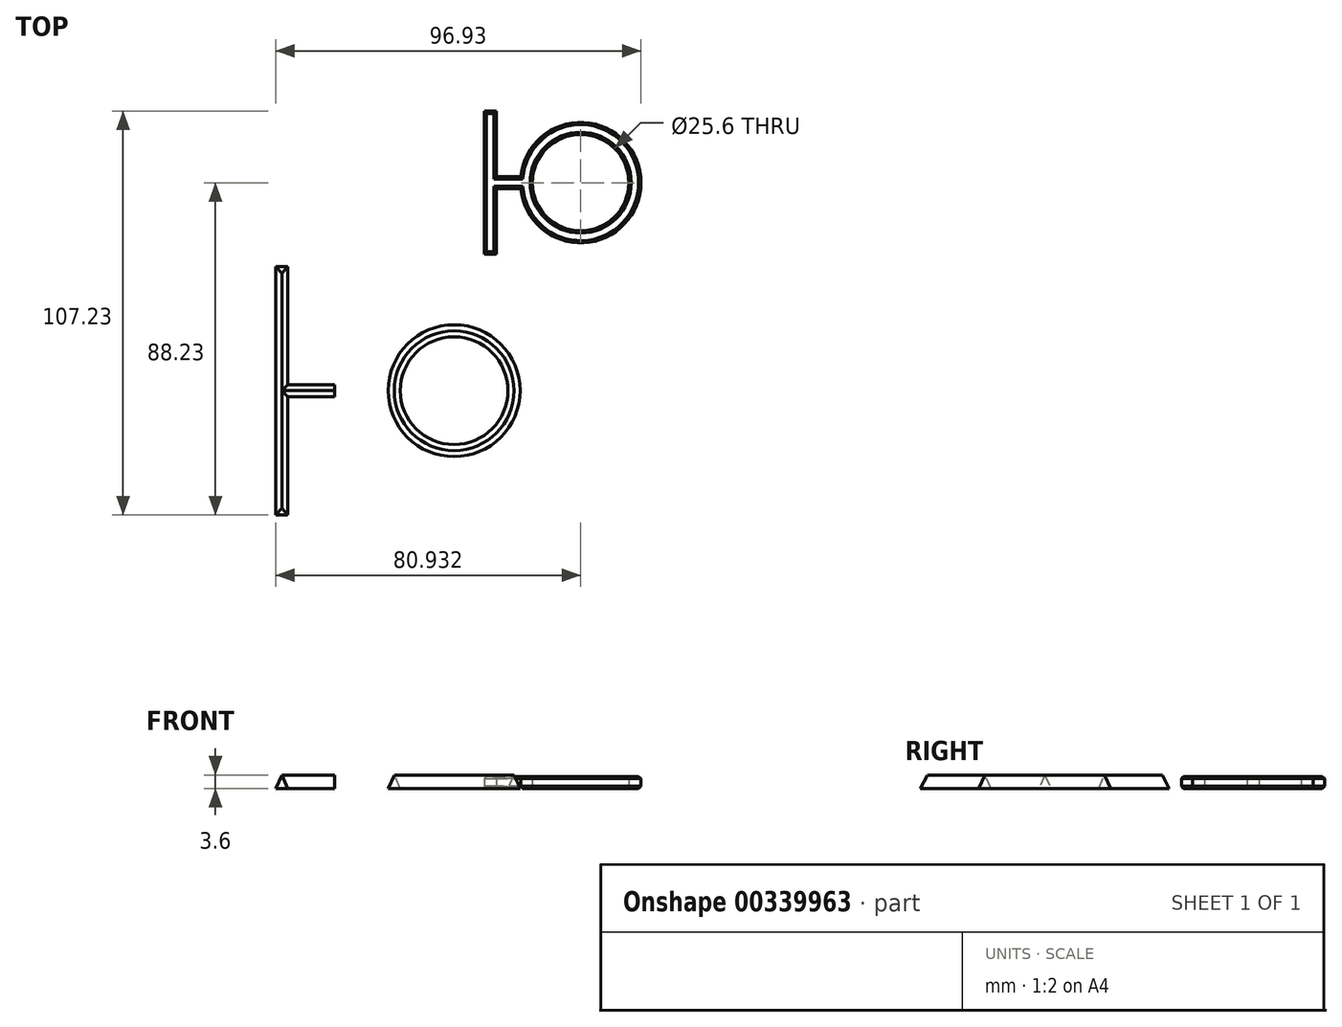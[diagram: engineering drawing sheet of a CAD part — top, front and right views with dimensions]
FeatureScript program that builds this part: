
annotation { "Feature Type Name" : "Feature", "Feature Type Description" : "" }
export const myFeature = defineFeature(function(context is Context, id is Id, definition is map)
    precondition{}
    {
        {
            var Q0;
            Q0=qCreatedBy(makeId("Top.planeOp"),FACE);
            var sketch = newSketch(context, id + "F0", { "sketchPlane" : qUnion([Q0])});
            skCircle(sketch, "E0", {"center": v(0, 0) * mm, "radius": 17.5 * mm});
            skCircle(sketch, "E1", {"center": v(0, 0) * mm, "radius": 14.3 * mm});
            skLineSegment(sketch, "E2.bottom", {"start": v(-45.75, 1.6) * mm, "end": v(-31.75, 1.6) * mm});
            skLineSegment(sketch, "E2.top", {"start": v(-45.75, -1.6) * mm, "end": v(-31.75, -1.6) * mm});
            skLineSegment(sketch, "E2.left", {"start": v(-45.75, 1.6) * mm, "end": v(-45.75, -1.6) * mm});
            skLineSegment(sketch, "E2.right", {"start": v(-31.75, 1.6) * mm, "end": v(-31.75, -1.6) * mm});
            skPoint(sketch, "E2.middle", {"position": v(-38.75, 0) * mm});
            skLineSegment(sketch, "E3.bottom", {"start": v(-47.35, 33) * mm, "end": v(-44.15, 33) * mm});
            skLineSegment(sketch, "E3.top", {"start": v(-47.35, -33) * mm, "end": v(-44.15, -33) * mm});
            skLineSegment(sketch, "E3.left", {"start": v(-47.35, 33) * mm, "end": v(-47.35, -33) * mm});
            skLineSegment(sketch, "E3.right", {"start": v(-44.15, 33) * mm, "end": v(-44.15, -33) * mm});
            skPoint(sketch, "E3.middle", {"position": v(-45.75, 0) * mm});
            skSolve(sketch);
        }
        {
            var Q0;
            Q0 = qSketchRegion(id + "F0", true);
            extrude(context, id + "F1", {"entities" : qUnion([Q0]), "depth" : 3.6 * mm, "offsetDistance" : 25 * mm});
        }
        {
            var Q0;
            Q0=makeQuery(id+"F1.opExtrude","CAP_EDGE",EDGE,{"disambiguationData":[OSD([sQuery(id+"F0.wireOp",EDGE,"E1")])],"isStart":false});
            var Q1;
            Q1=makeQuery(id+"F1.opExtrude","CAP_EDGE",EDGE,{"disambiguationData":[OSD([sQuery(id+"F0.wireOp",EDGE,"E0")])],"isStart":false});
            chamfer(context, id + "F2", {"entities" : qUnion([Q0, Q1]), "chamferType" : ChamferType.TWO_OFFSETS, "width1" : 3.6 * mm, "oppositeDirection" : false, "width2" : 1.6 * mm, "tangentPropagation" : true});
        }
        {
            var Q0;
            Q0=makeQuery(id+"F1.opExtrude","CAP_EDGE",EDGE,{"disambiguationData":[OSD([sQuery(id+"F0.wireOp",EDGE,"E3.top")])],"isStart":false});
            var Q1;
            Q1=makeQuery(id+"F1.opExtrude","CAP_EDGE",EDGE,{"disambiguationData":[OSD([sQuery(id+"F0.wireOp",EDGE,"E3.bottom")])],"isStart":false});
            chamfer(context, id + "F3", {"entities" : qUnion([Q0, Q1]), "chamferType" : ChamferType.TWO_OFFSETS, "width1" : 1.8 * mm, "oppositeDirection" : false, "width2" : 3.6 * mm, "tangentPropagation" : true});
        }
        {
            var Q0;
            Q0=makeQuery(id+"F1.opExtrude","CAP_EDGE",EDGE,{"disambiguationData":[OSD([sQuery(id+"F0.wireOp",EDGE,"E3.left")])],"isStart":false});
            var Q1;
            {var subQ0=sQuery(id+"F0.wireOp",EDGE,"E3.right");Q1=makeQuery(id+"F1.opExtrude","CAP_EDGE",EDGE,{"disambiguationData":[OSD([subQ0]),TDD([makeQuery(id+"F0.imprint","IMPRINT",EDGE,{"disambiguationData":[TD([[makeQuery(id+"F0.imprint","INTERSECT",VERTEX,{"derivedFrom":[sQuery(id+"F0.wireOp",EDGE,"E3.bottom"),subQ0]}),-1.0]])],"derivedFrom":subQ0})])],"isStart":false});}
            var Q2;
            {var subQ0=sQuery(id+"F0.wireOp",EDGE,"E3.right");Q2=makeQuery(id+"F1.opExtrude","CAP_EDGE",EDGE,{"disambiguationData":[OSD([subQ0]),TDD([makeQuery(id+"F0.imprint","IMPRINT",EDGE,{"disambiguationData":[TD([[makeQuery(id+"F0.imprint","INTERSECT",VERTEX,{"derivedFrom":[sQuery(id+"F0.wireOp",EDGE,"E3.top"),subQ0]}),1.0]])],"derivedFrom":subQ0})])],"isStart":false});}
            var Q3;
            Q3=makeQuery(id+"F1.opExtrude","CAP_EDGE",EDGE,{"disambiguationData":[OSD([sQuery(id+"F0.wireOp",EDGE,"E2.top")])],"isStart":false});
            var Q4;
            Q4=makeQuery(id+"F1.opExtrude","CAP_EDGE",EDGE,{"disambiguationData":[OSD([sQuery(id+"F0.wireOp",EDGE,"E2.bottom")])],"isStart":false});
            chamfer(context, id + "F4", {"entities" : qUnion([Q0, Q1, Q2, Q3, Q4]), "chamferType" : ChamferType.TWO_OFFSETS, "width1" : 1.6 * mm, "oppositeDirection" : false, "width2" : 3.6 * mm, "tangentPropagation" : true});
        }
        {
            var Q0;
            Q0=qCreatedBy(makeId("Top.planeOp"),FACE);
            var sketch = newSketch(context, id + "F5", { "sketchPlane" : qUnion([Q0])});
            skCircle(sketch, "E4", {"center": v(33.58, 55.23) * mm, "radius": 16 * mm});
            skCircle(sketch, "E5", {"center": v(33.58, 55.23) * mm, "radius": 12.8 * mm});
            skLineSegment(sketch, "E6.bottom", {"start": v(9.58, 56.83) * mm, "end": v(25.58, 56.83) * mm});
            skLineSegment(sketch, "E6.top", {"start": v(9.58, 53.63) * mm, "end": v(25.58, 53.63) * mm});
            skLineSegment(sketch, "E6.left", {"start": v(9.58, 56.83) * mm, "end": v(9.58, 53.63) * mm});
            skLineSegment(sketch, "E6.right", {"start": v(25.58, 56.83) * mm, "end": v(25.58, 53.63) * mm});
            skPoint(sketch, "E6.middle", {"position": v(17.58, 55.23) * mm});
            skLineSegment(sketch, "E7.bottom", {"start": v(11.18, 36.23) * mm, "end": v(7.98, 36.23) * mm});
            skLineSegment(sketch, "E7.top", {"start": v(11.18, 74.23) * mm, "end": v(7.98, 74.23) * mm});
            skLineSegment(sketch, "E7.left", {"start": v(11.18, 36.23) * mm, "end": v(11.18, 74.23) * mm});
            skLineSegment(sketch, "E7.right", {"start": v(7.98, 36.23) * mm, "end": v(7.98, 74.23) * mm});
            skPoint(sketch, "E7.middle", {"position": v(9.58, 55.23) * mm});
            skSolve(sketch);
        }
        {
            var Q0;
            Q0 = qSketchRegion(id + "F5", true);
            extrude(context, id + "F6", {"entities" : qUnion([Q0]), "depth" : 3.2 * mm, "offsetDistance" : 25 * mm});
        }
        {
            var Q0;
            Q0=makeQuery(id+"F6.opExtrude","CAP_FACE",FACE,{"disambiguationData":[OSD([sQuery(id+"F5.wireOp",EDGE,"E4"),sQuery(id+"F5.wireOp",EDGE,"E5"),sQuery(id+"F5.wireOp",EDGE,"E6.bottom"),sQuery(id+"F5.wireOp",EDGE,"E6.top"),sQuery(id+"F5.wireOp",EDGE,"E7.bottom"),sQuery(id+"F5.wireOp",EDGE,"E7.top"),sQuery(id+"F5.wireOp",EDGE,"E7.left"),sQuery(id+"F5.wireOp",EDGE,"E7.right")])],"isStart":false});
            var Q1;
            Q1=makeQuery(id+"F6.opExtrude","CAP_FACE",FACE,{"disambiguationData":[OSD([sQuery(id+"F5.wireOp",EDGE,"E4"),sQuery(id+"F5.wireOp",EDGE,"E5"),sQuery(id+"F5.wireOp",EDGE,"E6.bottom"),sQuery(id+"F5.wireOp",EDGE,"E6.top"),sQuery(id+"F5.wireOp",EDGE,"E7.bottom"),sQuery(id+"F5.wireOp",EDGE,"E7.top"),sQuery(id+"F5.wireOp",EDGE,"E7.left"),sQuery(id+"F5.wireOp",EDGE,"E7.right")])],"isStart":true});
            chamfer(context, id + "F7", {"entities" : qUnion([Q0, Q1]), "width" : 0.6 * mm, "tangentPropagation" : true});
        }
    });
